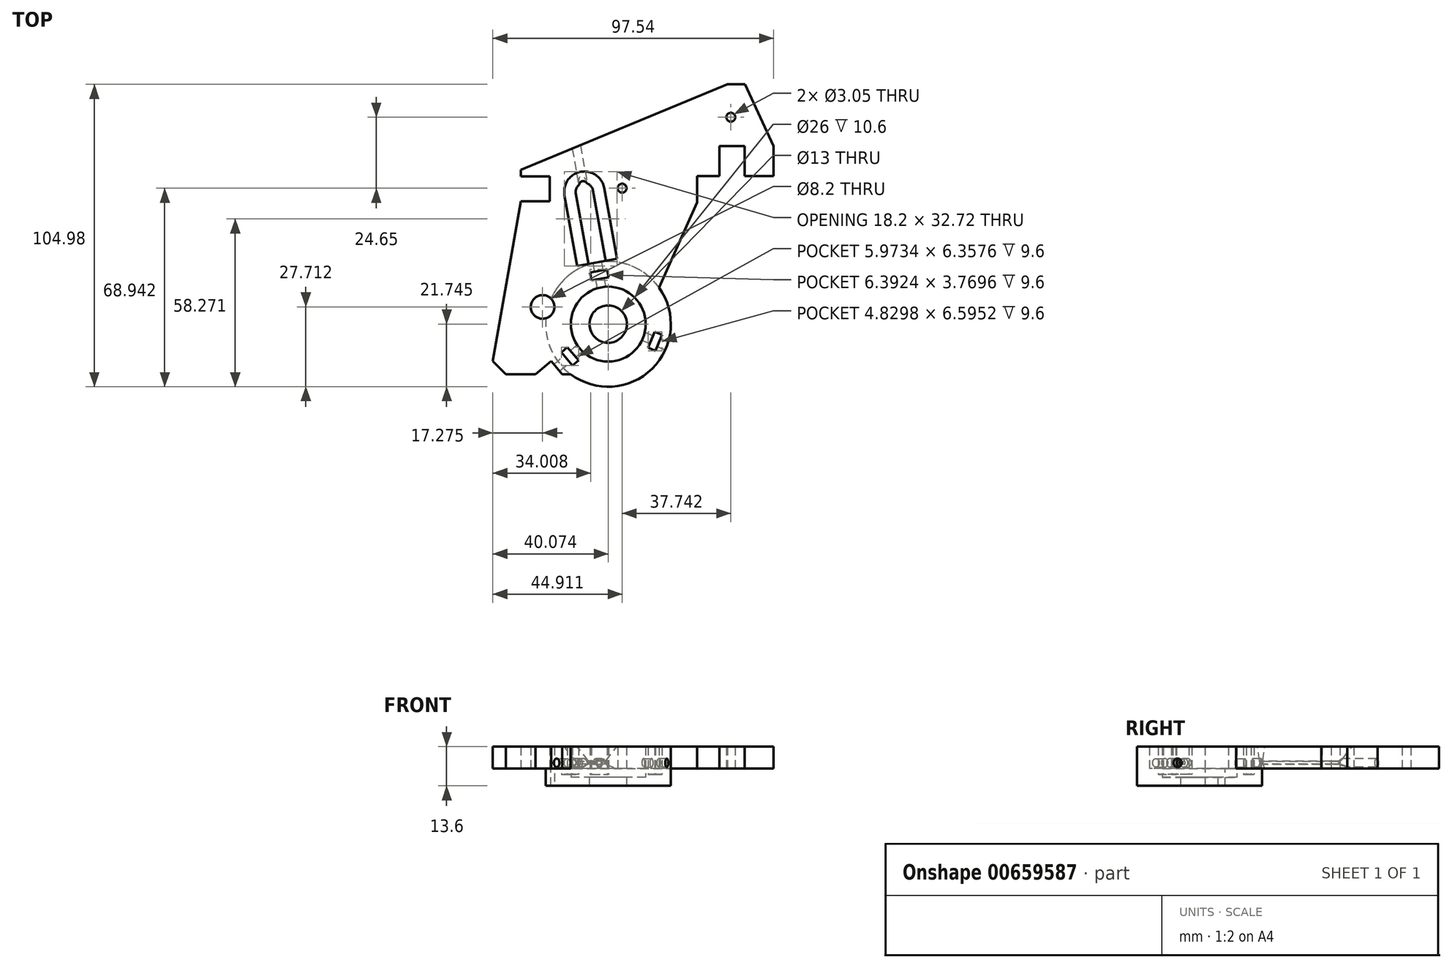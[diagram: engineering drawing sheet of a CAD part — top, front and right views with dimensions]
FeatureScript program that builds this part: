
annotation { "Feature Type Name" : "Feature", "Feature Type Description" : "" }
export const myFeature = defineFeature(function(context is Context, id is Id, definition is map)
    precondition{}
    {
        {
            var Q0;
            Q0=qCreatedBy(makeId("Top.planeOp"),FACE);
            var sketch = newSketch(context, id + "F0", { "sketchPlane" : qUnion([Q0])});
            skLineSegment(sketch, "E0", {"start": v(11.47, 17.6) * mm, "end": v(21.5, 17.6) * mm});
            skLineSegment(sketch, "E1", {"start": v(11.47, 17.6) * mm, "end": v(11.47, 28.1) * mm});
            skLineSegment(sketch, "E2", {"start": v(11.47, 28.1) * mm, "end": v(2.72, 28.1) * mm});
            skLineSegment(sketch, "E3", {"start": v(2.72, 28.1) * mm, "end": v(2.72, 17.6) * mm});
            skLineSegment(sketch, "E4", {"start": v(2.72, 17.6) * mm, "end": v(-5.03, 17.6) * mm});
            skLineSegment(sketch, "E5", {"start": v(-5.03, 17.6) * mm, "end": v(-5.03, 8.5) * mm});
            skLineSegment(sketch, "E6", {"start": v(21.5, 17.6) * mm, "end": v(21.5, 28.1) * mm});
            skLineSegment(sketch, "E7", {"start": v(21.5, 28.1) * mm, "end": v(11.51, 49.47) * mm});
            skLineSegment(sketch, "E8", {"start": v(11.51, 49.47) * mm, "end": v(5.46, 49.47) * mm});
            skLineSegment(sketch, "E9", {"start": v(-66.28, 17.52) * mm, "end": v(-66.28, 19.82) * mm});
            skLineSegment(sketch, "E10", {"start": v(-66.28, 19.82) * mm, "end": v(5.46, 49.47) * mm});
            skLineSegment(sketch, "E11", {"start": v(-66.28, 17.52) * mm, "end": v(-56.28, 17.52) * mm});
            skLineSegment(sketch, "E12", {"start": v(-56.28, 17.52) * mm, "end": v(-56.28, 8.82) * mm});
            skLineSegment(sketch, "E13", {"start": v(-56.28, 8.82) * mm, "end": v(-66.28, 8.82) * mm});
            skLineSegment(sketch, "E14", {"start": v(-76.03, -46.63) * mm, "end": v(-71.43, -51.23) * mm});
            skLineSegment(sketch, "E15", {"start": v(-76.03, -46.63) * mm, "end": v(-66.28, 8.82) * mm});
            skLineSegment(sketch, "E16", {"start": v(-51.92, -51.19) * mm, "end": v(-48.98, -51.18) * mm});
            skLineSegment(sketch, "E17", {"start": v(-5.03, 8.5) * mm, "end": v(-18.3, -21.06) * mm});
            skCircle(sketch, "E18", {"center": v(-31.12, 13.43) * mm, "radius": 1.52 * mm});
            skCircle(sketch, "E19", {"center": v(6.62, 38.08) * mm, "radius": 1.52 * mm});
            skPoint(sketch, "E19.centerSnap0", {"position": v(6.63, 38.08) * mm});
            skCircle(sketch, "E20", {"center": v(-58.76, -27.8) * mm, "radius": 4.1 * mm});
            skCircle(sketch, "E21", {"center": v(-35.96, -33.76) * mm, "radius": 6.5 * mm});
            skCircle(sketch, "E22", {"center": v(-35.96, -33.76) * mm, "radius": 13 * mm});
            skArc(sketch, "E23", {"start": v(-57.61, -31.74) * mm, "mid": v(-14.91, -39.27) * mm, "end": v(-55.83, -24.93) * mm});
            skLineSegment(sketch, "E24", {"start": v(-23.72, -38.17) * mm, "end": v(-20.9, -39.18) * mm, "construction": true});
            skLineSegment(sketch, "E25", {"start": v(-15.5, -41.13) * mm, "end": v(-18.31, -40.11) * mm, "construction": true});
            skLineSegment(sketch, "E26", {"start": v(-19.76, -36.42) * mm, "end": v(-17.22, -37.46) * mm});
            skLineSegment(sketch, "E27", {"start": v(-17.22, -37.46) * mm, "end": v(-19.5, -43.01) * mm});
            skLineSegment(sketch, "E28", {"start": v(-19.76, -36.42) * mm, "end": v(-22.05, -41.96) * mm});
            skLineSegment(sketch, "E29", {"start": v(-22.05, -41.96) * mm, "end": v(-19.5, -43.01) * mm});
            skLineSegment(sketch, "E30", {"start": v(-38.26, -20.97) * mm, "end": v(-38.8, -18.02) * mm, "construction": true});
            skLineSegment(sketch, "E31", {"start": v(-39.8, -12.36) * mm, "end": v(-39.28, -15.31) * mm, "construction": true});
            skLineSegment(sketch, "E32", {"start": v(-42.23, -15.84) * mm, "end": v(-41.74, -18.55) * mm});
            skLineSegment(sketch, "E33", {"start": v(-41.74, -18.55) * mm, "end": v(-35.84, -17.49) * mm});
            skLineSegment(sketch, "E34", {"start": v(-35.84, -17.49) * mm, "end": v(-36.33, -14.78) * mm});
            skLineSegment(sketch, "E35", {"start": v(-42.23, -15.84) * mm, "end": v(-36.33, -14.78) * mm});
            skLineSegment(sketch, "E36", {"start": v(-45.88, -42.16) * mm, "end": v(-48.18, -44.1) * mm, "construction": true});
            skLineSegment(sketch, "E37", {"start": v(-52.57, -47.8) * mm, "end": v(-50.28, -45.87) * mm, "construction": true});
            skLineSegment(sketch, "E38", {"start": v(-46.24, -46.38) * mm, "end": v(-48.34, -48.16) * mm});
            skLineSegment(sketch, "E39", {"start": v(-48.34, -48.16) * mm, "end": v(-52.21, -43.58) * mm});
            skLineSegment(sketch, "E40", {"start": v(-52.21, -43.58) * mm, "end": v(-50.11, -41.8) * mm});
            skLineSegment(sketch, "E41", {"start": v(-50.11, -41.8) * mm, "end": v(-46.24, -46.38) * mm});
            skLineSegment(sketch, "E42", {"start": v(-36.86, -11.83) * mm, "end": v(-42.76, -12.9) * mm});
            skLineSegment(sketch, "E43", {"start": v(-42.76, -12.9) * mm, "end": v(-47.2, 11.71) * mm});
            skLineSegment(sketch, "E44", {"start": v(-36.86, -11.83) * mm, "end": v(-41.29, 12.78) * mm});
            skArc(sketch, "E45", {"start": v(-41.28, 12.75) * mm, "mid": v(-44.77, 15.18) * mm, "end": v(-47.19, 11.69) * mm});
            skLineSegment(sketch, "E46", {"start": v(-48.34, -48.16) * mm, "end": v(-51.92, -51.19) * mm, "construction": true});
            skLineSegment(sketch, "E47", {"start": v(-55.8, -46.6) * mm, "end": v(-52.21, -43.58) * mm, "construction": true});
            skLineSegment(sketch, "E48", {"start": v(-51.92, -51.19) * mm, "end": v(-55.8, -46.6) * mm});
            skLineSegment(sketch, "E49", {"start": v(-55.8, -46.6) * mm, "end": v(-61.22, -51.19) * mm});
            skLineSegment(sketch, "E50", {"start": v(-71.43, -51.23) * mm, "end": v(-61.22, -51.19) * mm});
            skSolve(sketch);
        }
        {
            var Q0;
            Q0=makeQuery(id+"F0.imprint","IMPRINT",FACE,{"disambiguationData":[TD([[makeQuery(id+"F0.imprint","IMPRINT",EDGE,{"derivedFrom":sQuery(id+"F0.wireOp",EDGE,"E0")}),1.0]])]});
            var Q1;
            Q1=makeQuery(id+"F0.imprint","IMPRINT",FACE,{"disambiguationData":[TD([[makeQuery(id+"F0.imprint","IMPRINT",EDGE,{"derivedFrom":sQuery(id+"F0.wireOp",EDGE,"E22")}),-1.0]])]});
            extrude(context, id + "F1", {"entities" : qUnion([Q0, Q1]), "depth" : 7.6 * mm, "offsetDistance" : 25 * mm});
        }
        {
            var Q0;
            Q0=makeQuery(id+"F0.imprint","IMPRINT",FACE,{"disambiguationData":[TD([[makeQuery(id+"F0.imprint","IMPRINT",EDGE,{"derivedFrom":sQuery(id+"F0.wireOp",EDGE,"E21")}),-1.0]])]});
            var Q1;
            Q1=makeQuery(id+"F0.imprint","IMPRINT",FACE,{"disambiguationData":[TD([[makeQuery(id+"F0.imprint","IMPRINT",EDGE,{"derivedFrom":sQuery(id+"F0.wireOp",EDGE,"E22")}),-1.0]])]});
            extrude(context, id + "F2", {"entities" : qUnion([Q0, Q1]), "operationType" : NewBodyOperationType.ADD, "oppositeDirection" : true, "depth" : 6 * mm, "offsetDistance" : 25 * mm});
        }
        {
            var Q0;
            Q0=makeQuery(id+"F0.imprint","IMPRINT",FACE,{"disambiguationData":[TD([[makeQuery(id+"F0.imprint","IMPRINT",EDGE,{"derivedFrom":sQuery(id+"F0.wireOp",EDGE,"E21")}),-1.0]])]});
            extrude(context, id + "F3", {"entities" : qUnion([Q0]), "operationType" : NewBodyOperationType.REMOVE, "oppositeDirection" : true, "depth" : 3 * mm, "offsetDistance" : 25 * mm});
        }
        {
            var Q0;
            Q0=makeQuery(id+"F0.imprint","IMPRINT",FACE,{"disambiguationData":[TD([[makeQuery(id+"F0.imprint","IMPRINT",EDGE,{"derivedFrom":sQuery(id+"F0.wireOp",EDGE,"E38")}),-1.0]])]});
            var Q1;
            Q1=makeQuery(id+"F0.imprint","IMPRINT",FACE,{"disambiguationData":[TD([[makeQuery(id+"F0.imprint","IMPRINT",EDGE,{"derivedFrom":sQuery(id+"F0.wireOp",EDGE,"E32")}),1.0]])]});
            var Q2;
            Q2=makeQuery(id+"F0.imprint","IMPRINT",FACE,{"disambiguationData":[TD([[makeQuery(id+"F0.imprint","IMPRINT",EDGE,{"derivedFrom":sQuery(id+"F0.wireOp",EDGE,"E26")}),-1.0]])]});
            extrude(context, id + "F4", {"entities" : qUnion([Q0, Q1, Q2]), "operationType" : NewBodyOperationType.ADD, "oppositeDirection" : true, "depth" : 6 * mm, "offsetDistance" : 25 * mm});
        }
        {
            var Q0;
            Q0=makeQuery(id+"F0.imprint","IMPRINT",FACE,{"disambiguationData":[TD([[makeQuery(id+"F0.imprint","IMPRINT",EDGE,{"derivedFrom":sQuery(id+"F0.wireOp",EDGE,"E32")}),1.0]])]});
            var Q1;
            Q1=makeQuery(id+"F0.imprint","IMPRINT",FACE,{"disambiguationData":[TD([[makeQuery(id+"F0.imprint","IMPRINT",EDGE,{"derivedFrom":sQuery(id+"F0.wireOp",EDGE,"E26")}),-1.0]])]});
            var Q2;
            Q2=makeQuery(id+"F0.imprint","IMPRINT",FACE,{"disambiguationData":[TD([[makeQuery(id+"F0.imprint","IMPRINT",EDGE,{"derivedFrom":sQuery(id+"F0.wireOp",EDGE,"E38")}),-1.0]])]});
            extrude(context, id + "F5", {"entities" : qUnion([Q0, Q1, Q2]), "operationType" : NewBodyOperationType.REMOVE, "oppositeDirection" : true, "depth" : 2 * mm, "offsetDistance" : 25 * mm});
        }
        {
            var Q0;
            Q0=makeQuery(id+"F1.opExtrude","CAP_EDGE",EDGE,{"disambiguationData":[OSD([sQuery(id+"F0.wireOp",EDGE,"E45")])],"isStart":false});
            var Q1;
            Q1=makeQuery(id+"F1.opExtrude","CAP_EDGE",EDGE,{"disambiguationData":[OSD([sQuery(id+"F0.wireOp",EDGE,"E44")])],"isStart":false});
            var Q2;
            Q2=makeQuery(id+"F1.opExtrude","CAP_EDGE",EDGE,{"disambiguationData":[OSD([sQuery(id+"F0.wireOp",EDGE,"E43")])],"isStart":false});
            chamfer(context, id + "F6", {"entities" : qUnion([Q0, Q1, Q2]), "chamferType" : ChamferType.TWO_OFFSETS, "width1" : 5 * mm, "oppositeDirection" : false, "width2" : 4 * mm, "tangentPropagation" : true});
        }
        {
            var Q0;
            Q0=makeQuery(id+"F1.opExtrude","CAP_EDGE",EDGE,{"disambiguationData":[OSD([sQuery(id+"F0.wireOp",EDGE,"E44")])],"isStart":true});
            var Q1;
            Q1=makeQuery(id+"F1.opExtrude","CAP_EDGE",EDGE,{"disambiguationData":[OSD([sQuery(id+"F0.wireOp",EDGE,"E43")])],"isStart":true});
            var Q2;
            Q2=makeQuery(id+"F1.opExtrude","CAP_EDGE",EDGE,{"disambiguationData":[OSD([sQuery(id+"F0.wireOp",EDGE,"E45")])],"isStart":true});
            chamfer(context, id + "F7", {"entities" : qUnion([Q0, Q1, Q2]), "chamferType" : ChamferType.TWO_OFFSETS, "width1" : 4 * mm, "oppositeDirection" : false, "width2" : 1.5 * mm, "tangentPropagation" : true});
        }
        {
            var Q0;
            {var subQ0=sQuery(id+"F0.wireOp",EDGE,"E35");Q0=makeQuery(id+"F5.boolean.opBoolean","MERGE",FACE,{"derivedFrom":[makeQuery(id+"F2.boolean.opBoolean","MERGE",FACE,{"derivedFrom":[makeQuery(id+"F1.opExtrude","SWEPT_FACE",FACE,{"disambiguationData":[OSD([subQ0])]}),makeQuery(id+"F2.opExtrude","SWEPT_FACE",FACE,{"disambiguationData":[OSD([subQ0])]})]}),makeQuery(id+"F5.opExtrude","SWEPT_FACE",FACE,{"disambiguationData":[OSD([subQ0])]})]});}
            var sketch = newSketch(context, id + "F8", { "sketchPlane" : qUnion([Q0])});
            skCircle(sketch, "E51", {"center": v(-41.37, 2) * mm, "radius": 1.5 * mm});
            skSolve(sketch);
        }
        {
            var Q0;
            {var subQ0=sQuery(id+"F0.wireOp",EDGE,"E27");Q0=makeQuery(id+"F5.boolean.opBoolean","MERGE",FACE,{"derivedFrom":[makeQuery(id+"F2.boolean.opBoolean","MERGE",FACE,{"derivedFrom":[makeQuery(id+"F1.opExtrude","SWEPT_FACE",FACE,{"disambiguationData":[OSD([subQ0])]}),makeQuery(id+"F2.opExtrude","SWEPT_FACE",FACE,{"disambiguationData":[OSD([subQ0])]})]}),makeQuery(id+"F5.opExtrude","SWEPT_FACE",FACE,{"disambiguationData":[OSD([subQ0])]})]});}
            var sketch = newSketch(context, id + "F9", { "sketchPlane" : qUnion([Q0])});
            skCircle(sketch, "E52", {"center": v(44.2, 2) * mm, "radius": 1.5 * mm});
            skSolve(sketch);
        }
        {
            var Q0;
            {var subQ0=sQuery(id+"F0.wireOp",EDGE,"E39");Q0=makeQuery(id+"F5.boolean.opBoolean","MERGE",FACE,{"derivedFrom":[makeQuery(id+"F2.boolean.opBoolean","MERGE",FACE,{"derivedFrom":[makeQuery(id+"F1.opExtrude","SWEPT_FACE",FACE,{"disambiguationData":[OSD([subQ0])]}),makeQuery(id+"F2.opExtrude","SWEPT_FACE",FACE,{"disambiguationData":[OSD([subQ0])]})]}),makeQuery(id+"F5.opExtrude","SWEPT_FACE",FACE,{"disambiguationData":[OSD([subQ0])]})]});}
            var sketch = newSketch(context, id + "F10", { "sketchPlane" : qUnion([Q0])});
            skCircle(sketch, "E53", {"center": v(-2.58, 2) * mm, "radius": 1.5 * mm});
            skSolve(sketch);
        }
        {
            var Q0;
            Q0=makeQuery(id+"F8.imprint","IMPRINT",FACE,{"disambiguationData":[TD([[makeQuery(id+"F8.imprint","IMPRINT",EDGE,{"derivedFrom":sQuery(id+"F8.wireOp",EDGE,"E51")}),1.0]])]});
            extrude(context, id + "F11", {"entities" : qUnion([Q0]), "operationType" : NewBodyOperationType.REMOVE, "oppositeDirection" : true, "depth" : 45 * mm, "offsetDistance" : 25 * mm});
        }
        {
            var Q0;
            Q0=makeQuery(id+"F8.imprint","IMPRINT",FACE,{"disambiguationData":[TD([[makeQuery(id+"F8.imprint","IMPRINT",EDGE,{"derivedFrom":sQuery(id+"F8.wireOp",EDGE,"E51")}),1.0]])]});
            extrude(context, id + "F12", {"entities" : qUnion([Q0]), "operationType" : NewBodyOperationType.REMOVE, "depth" : 10 * mm, "offsetDistance" : 25 * mm});
        }
        {
            var Q0;
            Q0=makeQuery(id+"F9.imprint","IMPRINT",FACE,{"disambiguationData":[TD([[makeQuery(id+"F9.imprint","IMPRINT",EDGE,{"derivedFrom":sQuery(id+"F9.wireOp",EDGE,"E52")}),1.0]])]});
            extrude(context, id + "F13", {"entities" : qUnion([Q0]), "operationType" : NewBodyOperationType.REMOVE, "oppositeDirection" : true, "depth" : 10 * mm, "offsetDistance" : 25 * mm});
        }
        {
            var Q0;
            Q0=makeQuery(id+"F9.imprint","IMPRINT",FACE,{"disambiguationData":[TD([[makeQuery(id+"F9.imprint","IMPRINT",EDGE,{"derivedFrom":sQuery(id+"F9.wireOp",EDGE,"E52")}),1.0]])]});
            extrude(context, id + "F14", {"entities" : qUnion([Q0]), "operationType" : NewBodyOperationType.REMOVE, "depth" : 10 * mm, "offsetDistance" : 25 * mm});
        }
        {
            var Q0;
            Q0=makeQuery(id+"F10.imprint","IMPRINT",FACE,{"disambiguationData":[TD([[makeQuery(id+"F10.imprint","IMPRINT",EDGE,{"derivedFrom":sQuery(id+"F10.wireOp",EDGE,"E53")}),1.0]])]});
            extrude(context, id + "F15", {"entities" : qUnion([Q0]), "operationType" : NewBodyOperationType.REMOVE, "oppositeDirection" : true, "depth" : 15 * mm, "offsetDistance" : 25 * mm});
        }
        {
            var Q0;
            Q0=makeQuery(id+"F10.imprint","IMPRINT",FACE,{"disambiguationData":[TD([[makeQuery(id+"F10.imprint","IMPRINT",EDGE,{"derivedFrom":sQuery(id+"F10.wireOp",EDGE,"E53")}),1.0]])]});
            extrude(context, id + "F16", {"entities" : qUnion([Q0]), "operationType" : NewBodyOperationType.REMOVE, "depth" : 10 * mm, "offsetDistance" : 25 * mm});
        }
    });
